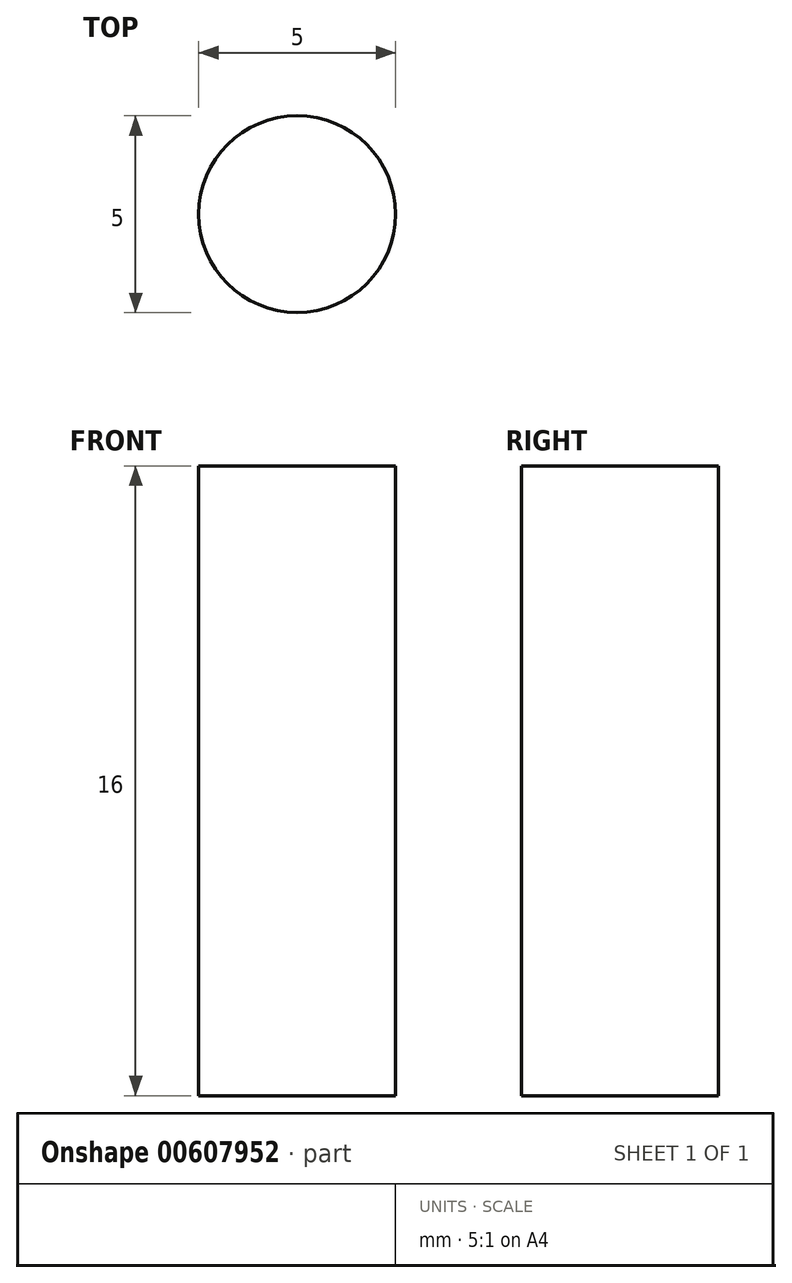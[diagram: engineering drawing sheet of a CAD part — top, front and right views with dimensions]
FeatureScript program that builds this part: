
annotation { "Feature Type Name" : "Feature", "Feature Type Description" : "" }
export const myFeature = defineFeature(function(context is Context, id is Id, definition is map)
    precondition{}
    {
        {
            var Q0;
            Q0=qCreatedBy(makeId("Top.planeOp"),FACE);
            var sketch = newSketch(context, id + "F0", { "sketchPlane" : qUnion([Q0])});
            skCircle(sketch, "E0", {"center": v(0, 0) * mm, "radius": 2.5 * mm});
            skSolve(sketch);
        }
        {
            var Q0;
            Q0=makeQuery(id+"F0.imprint","IMPRINT",FACE,{"disambiguationData":[TD([[makeQuery(id+"F0.imprint","IMPRINT",EDGE,{"derivedFrom":sQuery(id+"F0.wireOp",EDGE,"E0")}),1.0]])]});
            extrude(context, id + "F1", {"entities" : qUnion([Q0]), "depth" : 16 * mm, "offsetDistance" : 25 * mm});
        }
    });
